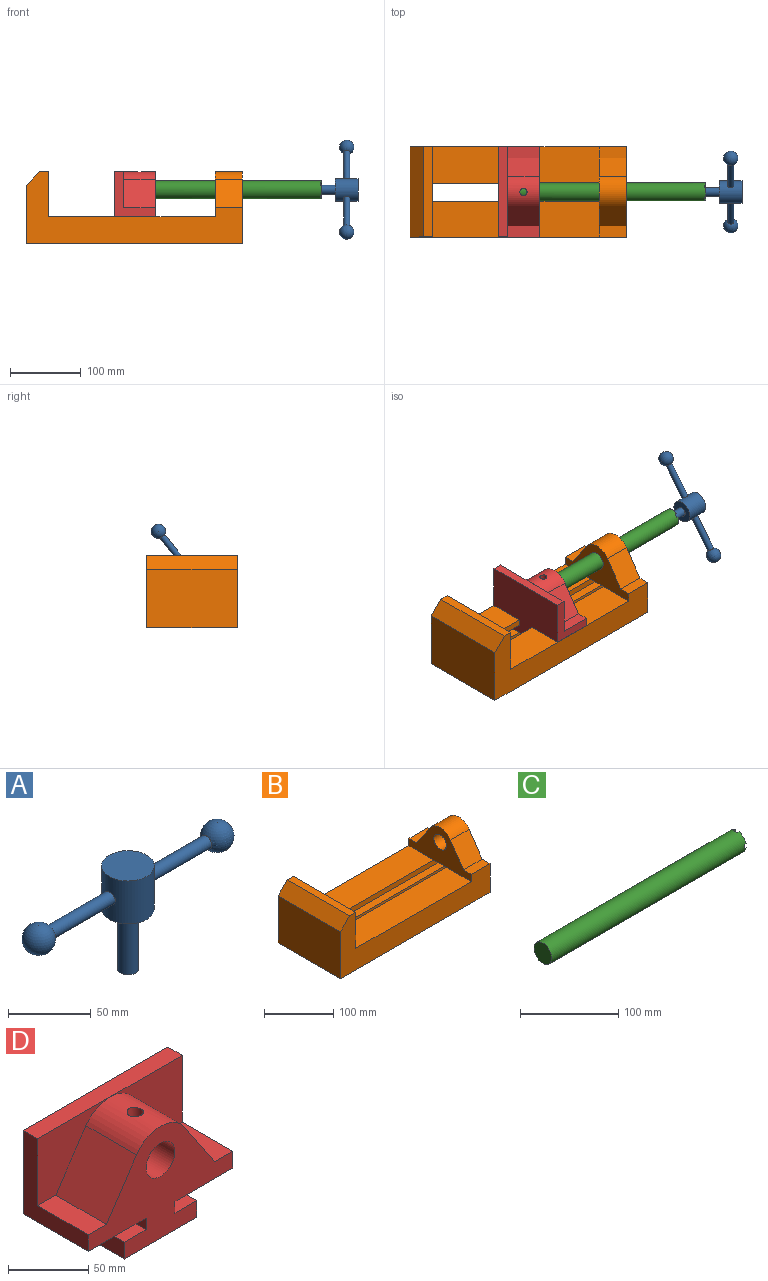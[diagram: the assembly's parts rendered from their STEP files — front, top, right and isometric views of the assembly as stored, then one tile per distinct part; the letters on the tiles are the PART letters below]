
ASSEMBLY  parts=4 mates=3
PART A: 9 faces, bbox 172.7x31.8x76.2 mm
  f0: cylinder r=4.45mm len=51.82mm, axis (-1,0,0), area 1438.5mm2, adj f1,f8
  f1: cylinder r=15.88mm len=31.75mm, axis (0,0,1), area 3041.6mm2, adj f0,f2,f3,f6
  f2: plane 31.75x31.75mm, normal (0,0,-1), area 665.1mm2, adj f1,f4
  f3: plane 31.75x31.75mm, normal (0,0,1), area 791.7mm2, adj f1
  f4: cylinder r=6.35mm len=44.45mm, axis (0,0,1), area 1773.5mm2, adj f2,f5
  f5: plane 12.7x12.7mm, normal (0,0,-1), area 126.7mm2, adj f4
  f6: cylinder r=4.45mm len=51.82mm, axis (-1,0,0), area 1438.5mm2, adj f1,f7
  f7: sphere r=10.16mm, area 1231.8mm2, adj f6
  f8: sphere r=10.16mm, area 1231.8mm2, adj f0
PART B: 28 faces, bbox 304.8x127x101.6 mm
  f0: plane 127x101.6mm, normal (1,0,0), area 7544.8mm2, adj f7,f8,f9,f11,f12,f13,f14,f15
  f1: plane 127x63.5mm, normal (-1,0,0), area 4157.7mm2, adj f2,f3,f8,f9,f16,f22,f23,f24
  f2: plane 234.95x50.8mm, normal (0,0,1), area 11935.5mm2, adj f1,f4,f9,f17
  f3: plane 234.95x50.8mm, normal (0,0,1), area 11935.5mm2, adj f1,f4,f8,f15
  f4: plane 127x101.6mm, normal (1,0,0), area 9516.1mm2, adj f2,f3,f5,f7,f8,f9,f11,f12
  f5: plane 127x12.7mm, normal (0,0,1), area 1612.9mm2, adj f4,f8,f9,f10
  f6: plane 127x82.55mm, normal (-1,0,0), area 10483.8mm2, adj f7,f8,f9,f10
  f7: plane 304.8x127mm, normal (0,0,-1), area 31774.1mm2, adj f0,f4,f6,f8,f9,f11,f21
  f8: plane 304.8x101.6mm, normal (0,1,0), area 13931.4mm2, adj f0,f1,f3,f4,f5,f6,f7,f10
  f9: plane 304.8x101.6mm, normal (0,-1,0), area 13931.4mm2, adj f0,f1,f2,f4,f5,f6,f7,f10
  f10: plane 127x19.05mm, normal (-0.71,0,0.71), area 3421.5mm2, adj f5,f6,f8,f9
  f11: plane 273.05x16.51mm, normal (0,-1,0), area 4508.1mm2, adj f0,f4,f7,f12
  f12: plane 273.05x19.05mm, normal (0,0,1), area 5201.6mm2, adj f0,f4,f11,f13
  f13: plane 273.05x12.7mm, normal (0,-1,0), area 3467.7mm2, adj f0,f4,f12,f14
  f14: plane 273.05x19.05mm, normal (0,0,-1), area 5201.6mm2, adj f0,f4,f13,f15
  f15: plane 273.05x8.89mm, normal (0,-1,0), area 2427.4mm2, adj f0,f3,f4,f14,f16
  f16: plane 38.1x25.4mm, normal (0,0,-1), area 967.7mm2, adj f0,f1,f15,f17
  f17: plane 273.05x8.89mm, normal (0,1,0), area 2427.4mm2, adj f0,f2,f4,f16,f18
  f18: plane 273.05x19.05mm, normal (0,0,-1), area 5201.6mm2, adj f0,f4,f17,f19
  f19: plane 273.05x12.7mm, normal (0,1,0), area 3467.7mm2, adj f0,f4,f18,f20
  f20: plane 273.05x19.05mm, normal (0,0,1), area 5201.6mm2, adj f0,f4,f19,f21
  f21: plane 273.05x16.51mm, normal (0,1,0), area 4508.1mm2, adj f0,f4,f7,f20
  f22: plane 38.1x15.88mm, normal (0,0,1), area 604.8mm2, adj f0,f1,f8,f24
  f23: cylinder r=25.4mm len=42.19mm, axis (1,0,0), area 1896.6mm2, adj f0,f1,f24,f26
  f24: plane 39.55x38.1mm, normal (0,0.83,0.56), area 1814.5mm2, adj f0,f1,f22,f23
  f25: plane 38.1x15.88mm, normal (0,0,1), area 604.8mm2, adj f0,f1,f9,f26
  f26: plane 39.55x38.1mm, normal (0,-0.83,0.56), area 1814.5mm2, adj f0,f1,f23,f25
  f27: cylinder r=12.7mm len=38.1mm, axis (1,0,0), area 3040.2mm2, adj f0,f1
PART C: 20 faces, bbox 279.4x25.4x25.4 mm
  f0: cylinder r=12.7mm len=279.4mm, axis (1,0,0), area 22243.2mm2, adj f1,f2,f3,f4,f5,f8,f9,f10
  f1: plane 9.9x9.9mm, normal (1,0,0), area 62.3mm2, adj f0,f6,f12,f17
  f2: plane 9.9x9.9mm, normal (1,0,0), area 62.3mm2, adj f0,f6,f9,f14
  f3: plane 9.9x9.9mm, normal (1,0,0), area 62.3mm2, adj f0,f6,f15,f18
  f4: plane 25.4x25.4mm, normal (-1,0,0), area 506.7mm2, adj f0
  f5: plane 9.9x9.9mm, normal (1,0,0), area 62.3mm2, adj f0,f6,f8,f13
  f6: cylinder r=6.35mm len=25.4mm, axis (1,0,0), area 960.3mm2, adj f1,f2,f3,f5,f7,f8,f9,f10
  f7: plane 12.7x12.7mm, normal (1,0,0), area 126.7mm2, adj f6
  f8: plane 6.62x2.54mm, normal (0,0,1), area 16.8mm2, adj f0,f5,f6,f10
  f9: plane 6.62x2.54mm, normal (0,0,-1), area 16.8mm2, adj f0,f2,f6,f10
  f10: plane 6.88x5.08mm, normal (1,0,0), area 32.7mm2, adj f0,f6,f8,f9
  f11: plane 6.88x5.08mm, normal (1,0,0), area 32.7mm2, adj f0,f6,f12,f13
  f12: plane 6.62x2.54mm, normal (0,1,0), area 16.8mm2, adj f0,f1,f6,f11
  f13: plane 6.62x2.54mm, normal (0,-1,0), area 16.8mm2, adj f0,f5,f6,f11
  f14: plane 6.62x2.54mm, normal (0,-1,0), area 16.8mm2, adj f0,f2,f6,f16
  f15: plane 6.62x2.54mm, normal (0,1,0), area 16.8mm2, adj f0,f3,f6,f16
  f16: plane 6.88x5.08mm, normal (1,0,0), area 32.7mm2, adj f0,f6,f14,f15
  f17: plane 6.62x2.54mm, normal (0,0,1), area 16.8mm2, adj f0,f1,f6,f19
  f18: plane 6.62x2.54mm, normal (0,0,-1), area 16.8mm2, adj f0,f3,f6,f19
  f19: plane 6.88x5.08mm, normal (1,0,0), area 32.7mm2, adj f0,f6,f17,f18
PART D: 24 faces, bbox 127x57.2x85.1 mm
  f0: cylinder r=12.7mm len=44.45mm, axis (0,1,0), area 3464.4mm2, adj f4,f22,f23
  f1: plane 44.45x15.88mm, normal (0,0,1), area 705.6mm2, adj f4,f8,f10,f19
  f2: plane 63.5x50.8mm, normal (0,-1,0), area 1700mm2, adj f7,f9,f11,f20,f21
  f3: plane 57.15x50.8mm, normal (0,0,-1), area 2903.2mm2, adj f4,f6,f10,f12
  f4: plane 127x85.09mm, normal (0,-1,0), area 5190mm2, adj f0,f1,f3,f5,f9,f10,f11,f12
  f5: plane 57.15x50.8mm, normal (0,0,-1), area 2903.2mm2, adj f4,f6,f11,f18
  f6: plane 127x85.09mm, normal (0,1,0), area 9096.8mm2, adj f3,f5,f7,f10,f11,f12,f13,f14
  f7: plane 127x12.7mm, normal (0,0,1), area 1612.9mm2, adj f2,f6,f8,f10,f11
  f8: plane 63.5x50.8mm, normal (0,-1,0), area 1700mm2, adj f1,f7,f10,f19,f21
  f9: plane 44.45x15.88mm, normal (0,0,1), area 705.6mm2, adj f2,f4,f11,f20
  f10: plane 63.5x57.15mm, normal (-1,0,0), area 1371mm2, adj f1,f3,f4,f6,f7,f8
  f11: plane 63.5x57.15mm, normal (1,0,0), area 1371mm2, adj f2,f4,f5,f6,f7,f9
  f12: plane 57.15x8.89mm, normal (-1,0,0), area 508.1mm2, adj f3,f4,f6,f13
  f13: plane 57.15x19.05mm, normal (0,0,1), area 1088.7mm2, adj f4,f6,f12,f14
  f14: plane 57.15x12.7mm, normal (-1,0,0), area 725.8mm2, adj f4,f6,f13,f15
  f15: plane 63.5x57.15mm, normal (0,0,-1), area 3629mm2, adj f4,f6,f14,f16
  f16: plane 57.15x12.7mm, normal (1,0,0), area 725.8mm2, adj f4,f6,f15,f17
  f17: plane 57.15x19.05mm, normal (0,0,1), area 1088.7mm2, adj f4,f6,f16,f18
  f18: plane 57.15x8.89mm, normal (1,0,0), area 508.1mm2, adj f4,f5,f6,f17
  f19: plane 44.45x39.55mm, normal (-0.83,0,0.56), area 2116.9mm2, adj f1,f4,f8,f21
  f20: plane 44.45x39.55mm, normal (0.83,0,0.56), area 2116.9mm2, adj f2,f4,f9,f21
  f21: cylinder r=25.4mm len=44.45mm, axis (0,1,0), area 2131.3mm2, adj f2,f4,f8,f19,f20,f23
  f22: plane 25.4x25.4mm, normal (0,-1,0), area 506.7mm2, adj f0
  f23: cylinder r=5.08mm len=13.76mm, axis (0,0,1), area 413.9mm2, adj f0,f21
PLACE A rot(axis=(0.69,0.24,0.69),153.1deg) t=(174.62,-10.34,131.9)mm
PLACE B t=(11.51,-73.84,55.7)mm fixed
PLACE C rot(axis=(1,0,0),141.6deg) t=(123.82,-10.34,131.9)mm
PLACE D rot(axis=(0,0,1),90deg) t=(-168.28,53.16,93.8)mm
MATE slider D.f6 <-> B.f4  axis (-1,0,0) through (-168.28,-23.04,93.8)mm
MATE revolute D.f0 <-> C.f0  axis (1,0,0) through (-155.58,-10.34,131.9)mm
MATE fastened C.f0 <-> A.f1  axis (1,0,0) through (98.42,-10.34,131.9)mm
